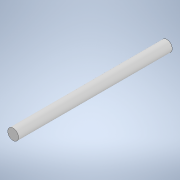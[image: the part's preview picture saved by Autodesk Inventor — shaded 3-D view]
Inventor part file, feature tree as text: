
AUTODESK INVENTOR PART (.ipt)
format: ipt  version: 2021 (Build 250183000, 183)  size: 102,400 bytes
history: native  units: mm
features: extrude x3, sketch x3
ambient origin geometry x8: Origin, YZ Plane, XZ Plane, XY Plane, X Axis, Y Axis, Z Axis, Center Point
bodies: Solid1 (feature_tree)
feature tree (6):
  extrude  "Extrusion1"  Depth=30.0mm TaperAngle=0.0deg
  extrude  "Extrusion3"  Depth=6.0mm TaperAngle=0.0deg
  extrude  "Extrusion4"  Depth=0.872665mm
  sketch  "Sketch1"  dims[d0=3.0mm d1=30.0mm d2=0.0mm]
  sketch  "Sketch4"  dims[d6=6.5mm d7=0.0mm d8=6.0mm d9=0.0mm]
  sketch  "Sketch5"  dims[d4=0.5mm d5=0.872665mm]
